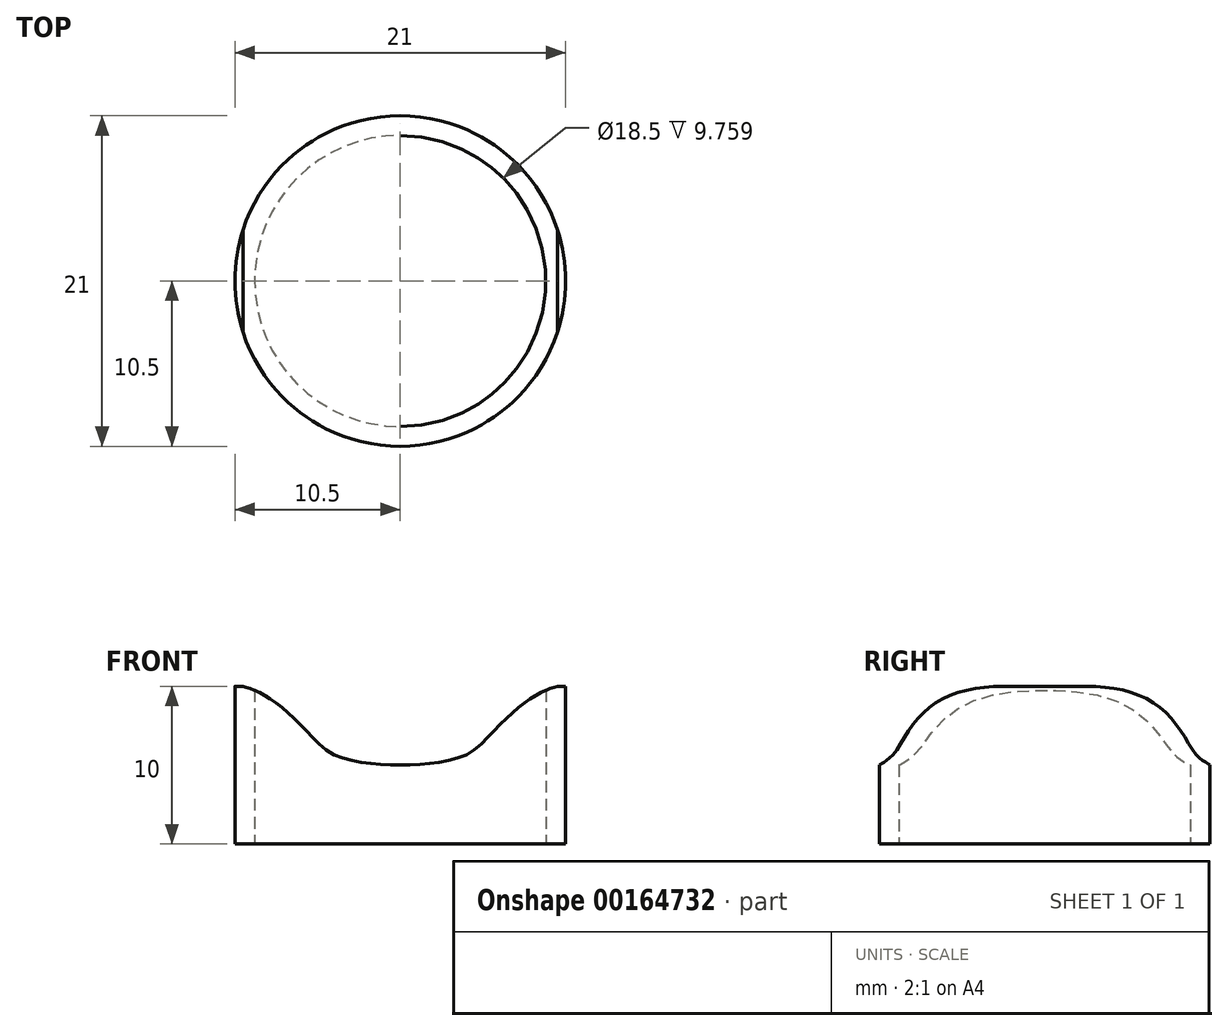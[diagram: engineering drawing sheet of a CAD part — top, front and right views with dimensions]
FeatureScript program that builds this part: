
annotation { "Feature Type Name" : "Feature", "Feature Type Description" : "" }
export const myFeature = defineFeature(function(context is Context, id is Id, definition is map)
    precondition{}
    {
        {
            var Q0;
            Q0=qCreatedBy(makeId("Top.planeOp"),FACE);
            var sketch = newSketch(context, id + "F0", { "sketchPlane" : qUnion([Q0])});
            skCircle(sketch, "E0", {"center": v(0, 0) * mm, "radius": 9.25 * mm});
            skCircle(sketch, "E1", {"center": v(0, 0) * mm, "radius": 10.5 * mm});
            skSolve(sketch);
        }
        {
            var Q0;
            Q0 = qSketchRegion(id + "F0", true);
            extrude(context, id + "F1", {"entities" : qUnion([Q0]), "depth" : 10 * mm});
        }
        {
            var Q0;
            Q0=qCreatedBy(makeId("Front.planeOp"),FACE);
            var sketch = newSketch(context, id + "F2", { "sketchPlane" : qUnion([Q0])});
            skFitSpline(sketch, "E2", {"points": [v(-11.24, 10.09) * mm, v(-8.48, 9.36) * mm, v(-5.73, 6.94) * mm, v(-4.07, 5.6) * mm, v(-1.52, 5.07) * mm, v(0, 5) * mm], "startDerivative": vector(12.73, 1.29) * mm, "endDerivative": vector(12.04, -0.05) * mm});
            skFitSpline(sketch, "E3.MirrorCS", {"points": [v(11.24, 10.09) * mm, v(8.48, 9.36) * mm, v(5.73, 6.94) * mm, v(4.07, 5.6) * mm, v(1.52, 5.07) * mm, v(0, 5) * mm], "startDerivative": vector(-12.73, 1.29) * mm, "endDerivative": vector(-12.04, -0.05) * mm});
            skLineSegment(sketch, "E4", {"start": v(-11.24, 10.09) * mm, "end": v(11.24, 10.09) * mm});
            skSolve(sketch);
        }
        {
            var Q0;
            Q0 = qSketchRegion(id + "F2", true);
            extrude(context, id + "F3", {"entities" : qUnion([Q0]), "operationType" : NewBodyOperationType.REMOVE, "endBound" : BoundingType.SYMMETRIC, "oppositeDirection" : true, "depth" : 25 * mm});
        }
    });
